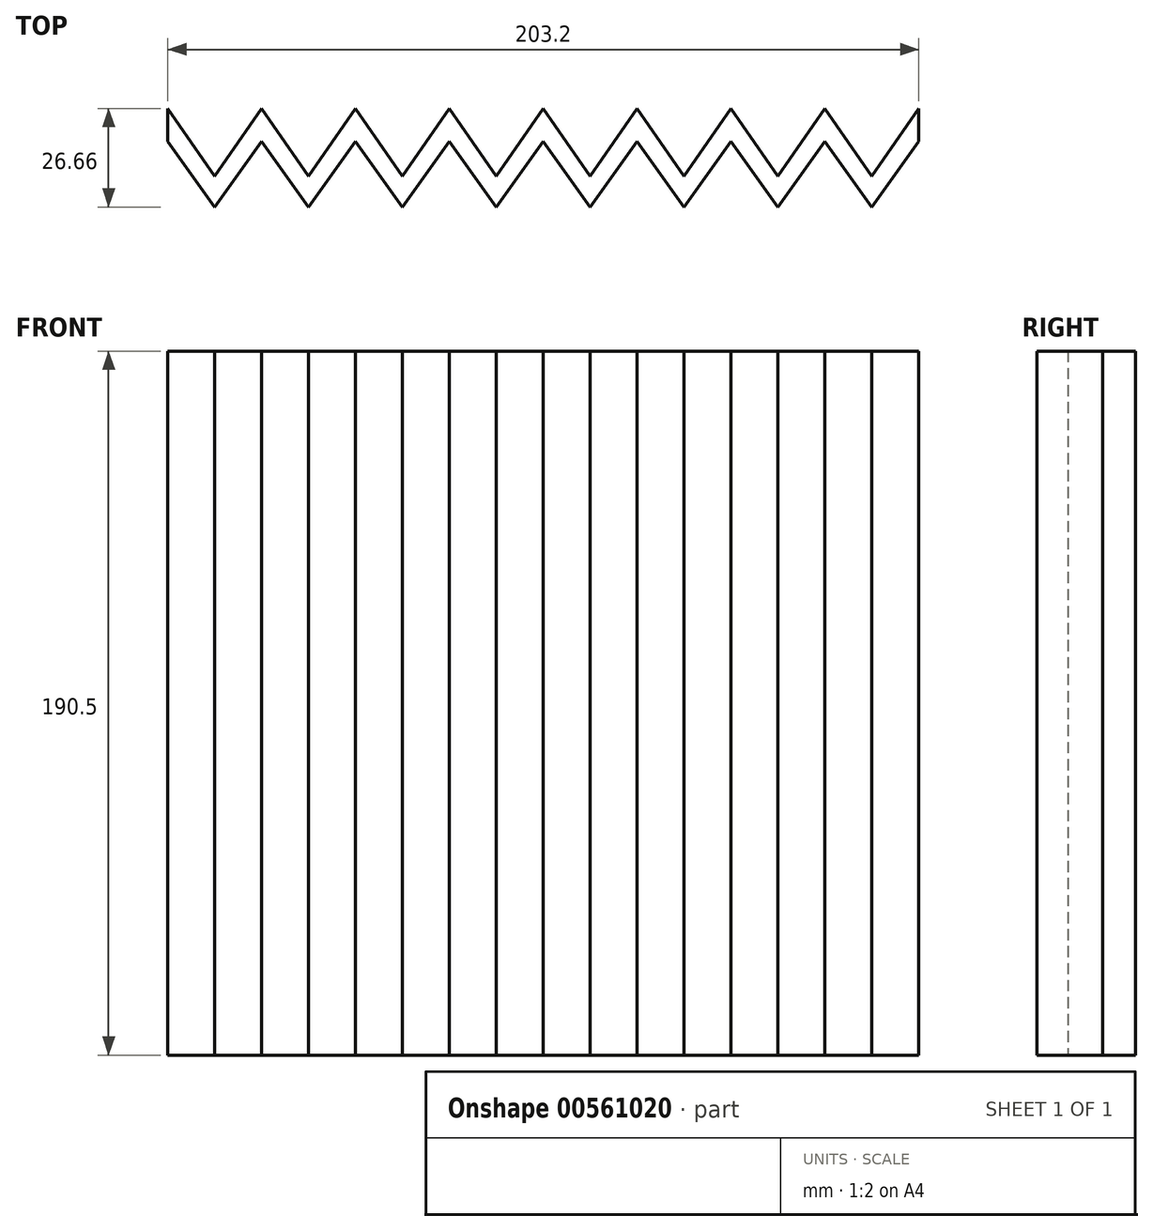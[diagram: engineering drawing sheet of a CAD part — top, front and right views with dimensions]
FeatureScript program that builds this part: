
annotation { "Feature Type Name" : "Feature", "Feature Type Description" : "" }
export const myFeature = defineFeature(function(context is Context, id is Id, definition is map)
    precondition{}
    {
        {
            var Q0;
            Q0=qCreatedBy(makeId("Top.planeOp"),FACE);
            var sketch = newSketch(context, id + "F0", { "sketchPlane" : qUnion([Q0])});
            skLineSegment(sketch, "E0", {"start": v(-63.5, 18.28) * mm, "end": v(-50.8, 0) * mm});
            skLineSegment(sketch, "E1", {"start": v(-63.5, 18.28) * mm, "end": v(-63.5, 9.37) * mm});
            skLineSegment(sketch, "E2", {"start": v(-50.8, 0) * mm, "end": v(-50.8, 9.66) * mm, "construction": true});
            skLineSegment(sketch, "E3", {"start": v(-50.8, 0) * mm, "end": v(-50.8, -8.38) * mm, "construction": true});
            skLineSegment(sketch, "E4", {"start": v(-63.5, 9.37) * mm, "end": v(-50.8, -8.38) * mm});
            skLineSegment(sketch, "E5.MirrorCS", {"start": v(-38.1, 9.37) * mm, "end": v(-50.8, -8.38) * mm});
            skLineSegment(sketch, "E6.MirrorCS", {"start": v(-38.1, 18.28) * mm, "end": v(-50.8, 0) * mm});
            skLineSegment(sketch, "E7", {"start": v(-38.1, 18.28) * mm, "end": v(-38.1, 9.37) * mm, "construction": true});
            skLineSegment(sketch, "E8.MirrorCS", {"start": v(-38.1, 9.37) * mm, "end": v(-25.4, -8.38) * mm});
            skLineSegment(sketch, "E9.MirrorCS", {"start": v(-38.1, 18.28) * mm, "end": v(-25.4, 0) * mm});
            skLineSegment(sketch, "E10.1.0.0", {"start": v(-12.7, 18.28) * mm, "end": v(-25.4, 0) * mm});
            skLineSegment(sketch, "E10.1.0.1", {"start": v(-12.7, 9.37) * mm, "end": v(-25.4, -8.38) * mm});
            skLineSegment(sketch, "E10.1.0.2", {"start": v(-12.7, 9.37) * mm, "end": v(0, -8.38) * mm});
            skLineSegment(sketch, "E10.1.0.3", {"start": v(-12.7, 18.28) * mm, "end": v(0, 0) * mm});
            skLineSegment(sketch, "E10.2.0.0", {"start": v(12.7, 18.28) * mm, "end": v(0, 0) * mm});
            skLineSegment(sketch, "E10.2.0.1", {"start": v(12.7, 9.37) * mm, "end": v(0, -8.38) * mm});
            skLineSegment(sketch, "E10.2.0.2", {"start": v(12.7, 9.37) * mm, "end": v(25.4, -8.38) * mm});
            skLineSegment(sketch, "E10.2.0.3", {"start": v(12.7, 18.28) * mm, "end": v(25.4, 0) * mm});
            skLineSegment(sketch, "E10.3.0.0", {"start": v(38.1, 18.28) * mm, "end": v(25.4, 0) * mm});
            skLineSegment(sketch, "E10.3.0.1", {"start": v(38.1, 9.37) * mm, "end": v(25.4, -8.38) * mm});
            skLineSegment(sketch, "E10.3.0.2", {"start": v(38.1, 9.37) * mm, "end": v(50.8, -8.38) * mm});
            skLineSegment(sketch, "E10.3.0.3", {"start": v(38.1, 18.28) * mm, "end": v(50.8, 0) * mm});
            skLineSegment(sketch, "E10.4.0.0", {"start": v(63.5, 18.28) * mm, "end": v(50.8, 0) * mm});
            skLineSegment(sketch, "E10.4.0.1", {"start": v(63.5, 9.37) * mm, "end": v(50.8, -8.38) * mm});
            skLineSegment(sketch, "E10.4.0.2", {"start": v(63.5, 9.37) * mm, "end": v(76.2, -8.38) * mm});
            skLineSegment(sketch, "E10.4.0.3", {"start": v(63.5, 18.28) * mm, "end": v(76.2, 0) * mm});
            skLineSegment(sketch, "E10.5.0.0", {"start": v(88.9, 18.28) * mm, "end": v(76.2, 0) * mm});
            skLineSegment(sketch, "E10.5.0.1", {"start": v(88.9, 9.37) * mm, "end": v(76.2, -8.38) * mm});
            skLineSegment(sketch, "E10.5.0.2", {"start": v(88.9, 9.37) * mm, "end": v(101.6, -8.38) * mm});
            skLineSegment(sketch, "E10.5.0.3", {"start": v(88.9, 18.28) * mm, "end": v(101.6, 0) * mm});
            skLineSegment(sketch, "E10.6.0.0", {"start": v(114.3, 18.28) * mm, "end": v(101.6, 0) * mm});
            skLineSegment(sketch, "E10.6.0.1", {"start": v(114.3, 9.37) * mm, "end": v(101.6, -8.38) * mm});
            skLineSegment(sketch, "E10.6.0.2", {"start": v(114.3, 9.37) * mm, "end": v(127, -8.38) * mm});
            skLineSegment(sketch, "E10.6.0.3", {"start": v(114.3, 18.28) * mm, "end": v(127, 0) * mm});
            skLineSegment(sketch, "E10.direction1", {"start": v(-50.8, 0) * mm, "end": v(-25.4, 0) * mm, "construction": true});
            skLineSegment(sketch, "E11", {"start": v(127, 0) * mm, "end": v(127, -8.38) * mm, "construction": true});
            skLineSegment(sketch, "E12.MirrorCS", {"start": v(139.7, 18.28) * mm, "end": v(127, 0) * mm});
            skLineSegment(sketch, "E13.MirrorCS", {"start": v(139.7, 9.37) * mm, "end": v(127, -8.38) * mm});
            skLineSegment(sketch, "E14", {"start": v(139.7, 18.28) * mm, "end": v(139.7, 9.37) * mm});
            skSolve(sketch);
        }
        {
            var Q0;
            Q0=makeQuery(id+"F0.imprint","IMPRINT",FACE,{"disambiguationData":[TD([[makeQuery(id+"F0.imprint","IMPRINT",EDGE,{"derivedFrom":sQuery(id+"F0.wireOp",EDGE,"E0")}),-1.0]])]});
            extrude(context, id + "F1", {"entities" : qUnion([Q0]), "depth" : 190.5 * mm, "offsetDistance" : 25.4 * mm});
        }
    });
